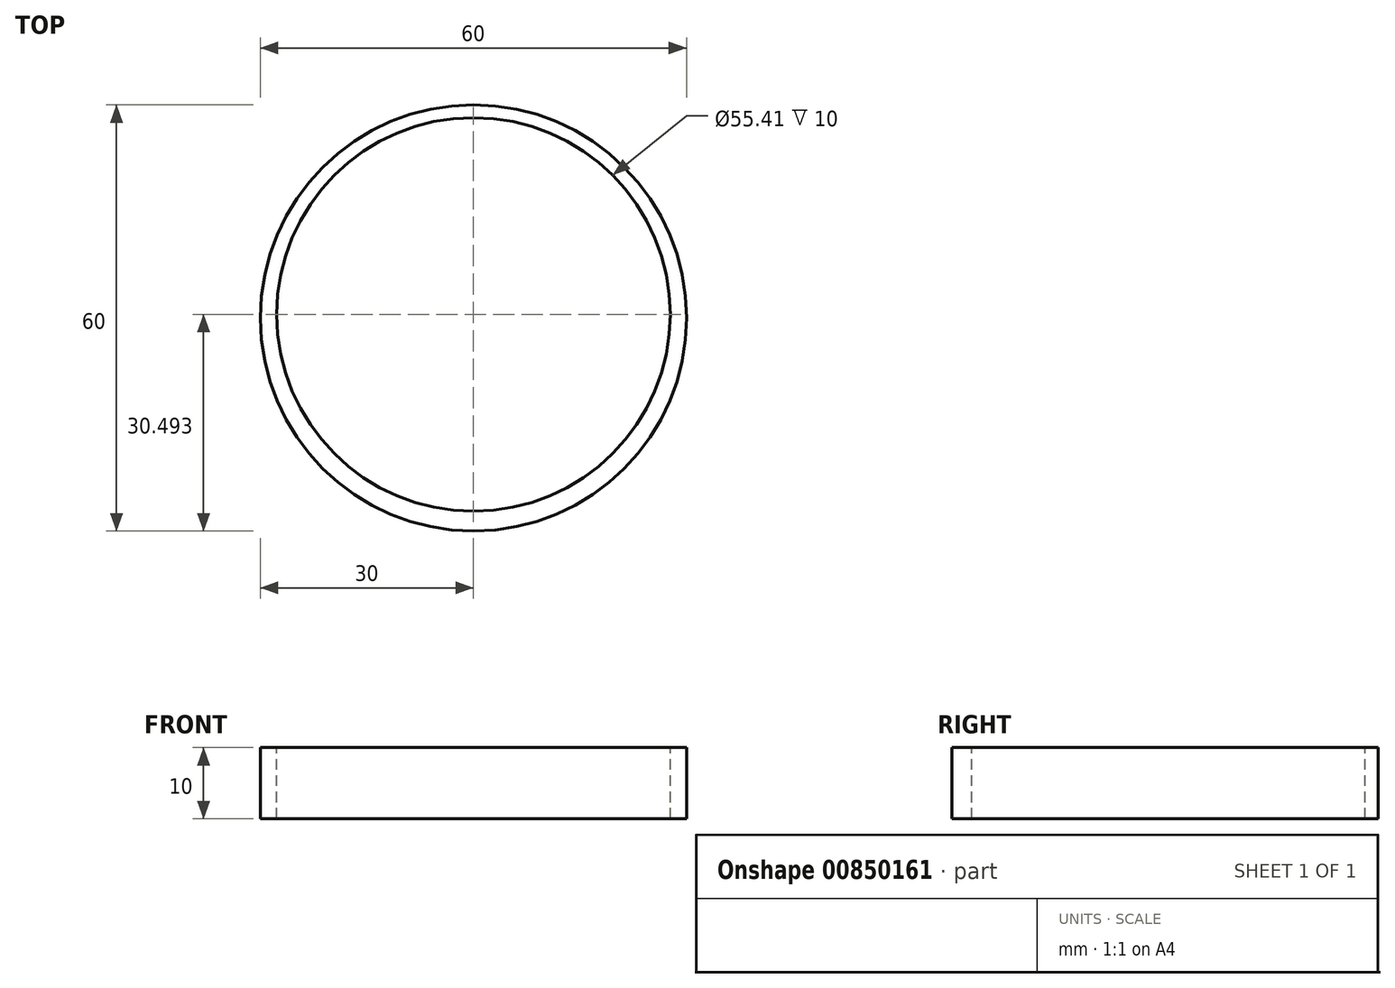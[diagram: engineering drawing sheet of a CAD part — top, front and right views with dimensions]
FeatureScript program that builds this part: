
annotation { "Feature Type Name" : "Feature", "Feature Type Description" : "" }
export const myFeature = defineFeature(function(context is Context, id is Id, definition is map)
    precondition{}
    {
        {
            var Q0;
            Q0=qCreatedBy(makeId("Top.planeOp"),FACE);
            var sketch = newSketch(context, id + "F0", { "sketchPlane" : qUnion([Q0])});
            skCircle(sketch, "E0", {"center": v(0, -6.03) * mm, "radius": 30 * mm});
            skSolve(sketch);
        }
        {
            var Q0;
            Q0=makeQuery(id+"F0.imprint","IMPRINT",FACE,{"disambiguationData":[TD([[makeQuery(id+"F0.imprint","IMPRINT",EDGE,{"derivedFrom":sQuery(id+"F0.wireOp",EDGE,"E0")}),1.0]])]});
            extrude(context, id + "F1", {"entities" : qUnion([Q0]), "depth" : 10 * mm, "offsetDistance" : 25.4 * mm});
        }
        {
            var Q0;
            Q0=makeQuery(id+"F1.opExtrude","CAP_FACE",FACE,{"disambiguationData":[OSD([sQuery(id+"F0.wireOp",EDGE,"E0")])],"isStart":false});
            var sketch = newSketch(context, id + "F2", { "sketchPlane" : qUnion([Q0])});
            skSolve(sketch);
        }
        {
            var Q0;
            Q0=makeQuery(id+"F2.imprint","IMPRINT",FACE,{"disambiguationData":[TD([[makeQuery(id+"F2.imprint","IMPRINT",EDGE,{"derivedFrom":makeQuery(id+"F1.opExtrude","CAP_EDGE",EDGE,{"disambiguationData":[OSD([sQuery(id+"F0.wireOp",EDGE,"E0")])],"isStart":false})}),1.0]])]});
            var sketch = newSketch(context, id + "F3", { "sketchPlane" : qUnion([Q0])});
            skCircle(sketch, "E1", {"center": v(0, -5.54) * mm, "radius": 27.7 * mm});
            skSolve(sketch);
        }
        {
            var Q0;
            Q0 = qSketchRegion(id + "F3", true);
            extrude(context, id + "F4", {"entities" : qUnion([Q0]), "operationType" : NewBodyOperationType.REMOVE, "oppositeDirection" : true, "depth" : 10 * mm, "offsetDistance" : 25.4 * mm});
        }
    });
